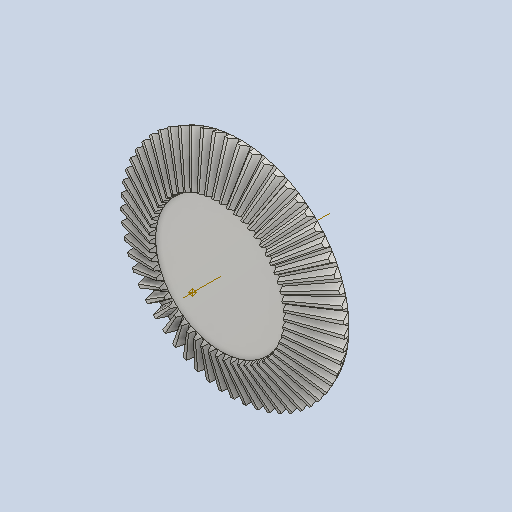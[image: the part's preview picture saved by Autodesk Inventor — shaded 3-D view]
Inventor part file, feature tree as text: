
AUTODESK INVENTOR PART (.ipt)
format: ipt  version: 2023 (Build 270158030, 158C)  size: 912,384 bytes
history: native  units: mm
features: other x24, loft x2, pattern_circular x2, sketch x1
ambient origin geometry x6: Origin, XZ Plane, X Axis, Y Axis, Z Axis, Center Point
bodies: Solid1 (feature_tree)
feature tree (29):
  other  "Top Point"
  other  "Mesh Plane2"
  other  "Teeth Body"
  other  "Start Point"
  other  "Tooth Plane"
  other  "Start Sketch"
  other  "End Point"
  other  "3D Sketch Right"
  other  "End Plane Right"
  loft  "Loft Right"
  pattern_circular  "Circular Pattern Right"  [2 undecoded]
  other  "3D Sketch Left"
  other  "End Plane Left"
  loft  "Loft Left"
  pattern_circular  "Circular Pattern Left"  [2 undecoded]
  other  "Fix Body"
  other  "Mesh Plane"
  other  "Top Plane"
  other  "Teeth Body Sketch"
  other  "End Plane"
  other  "End Sketch"
  other  "Helical Curve Left"
  other  "End Sketch Left"
  other  "Body Sketch"
  sketch  "Sketch6"  dims[d0=171.0mm d1=168.305803mm d2=173.245164mm d3=36.8mm d4=31.717949mm d5=90.0deg d7=79.194946mm d8=76.874908mm d9=201.595668mm d11=37.13mm d12=47.301593mm d15=45.91588mm d16=120.409151mm d17=0.0mm d18=90.0deg d19=0.0mm d20=90.0deg d21=570.0mm d22=360.0deg d26=442.07937mm d27=13.893824mm d28=171.0mm d29=-11.872688mm d30=47.301593mm d31=45.91588mm d32=120.409151mm d35=0.0mm d37=0.0mm d39=0.0mm d40=90.0deg d41=570.0mm d42=360.0deg d46=90.0deg d47=90.0deg d48=0.0mm d49=0.0mm d50=90.0deg d51=0.551157mm d52=0.0mm d53=0.0mm d54=0.0mm d56=19.532028mm d57=233.471083mm d58=224.099083mm d59=139.447713mm d60=133.850001mm d61=139.447713mm d62=133.850001mm d65=442.07937mm d66=31.5mm d67=171.0mm d68=-11.872688mm d69=13.893824mm d70=45.91588mm d71=120.409151mm d72=47.301593mm d73=133.850001mm d74=139.447713mm d75=0.0mm d77=0.0mm d79=0.0mm d80=90.0deg d81=570.0mm d82=360.0deg d84=10.0mm d85=20.0mm d86=20.0mm d87=10.0mm d88=0.0mm d89=0.0mm d90=90.0deg d91=90.0deg d92=90.0deg d93=90.0deg]
  other  "Srf1"
  other  "Helical Curve Right"
  other  "End Sketch Right"
  other  "Pitch Diameter"
note: 4 required parameter values undecoded (feature->parameter linkage not recoverable at this tier; creation-order binding heuristic only, values carry confidence <= 0.55)
